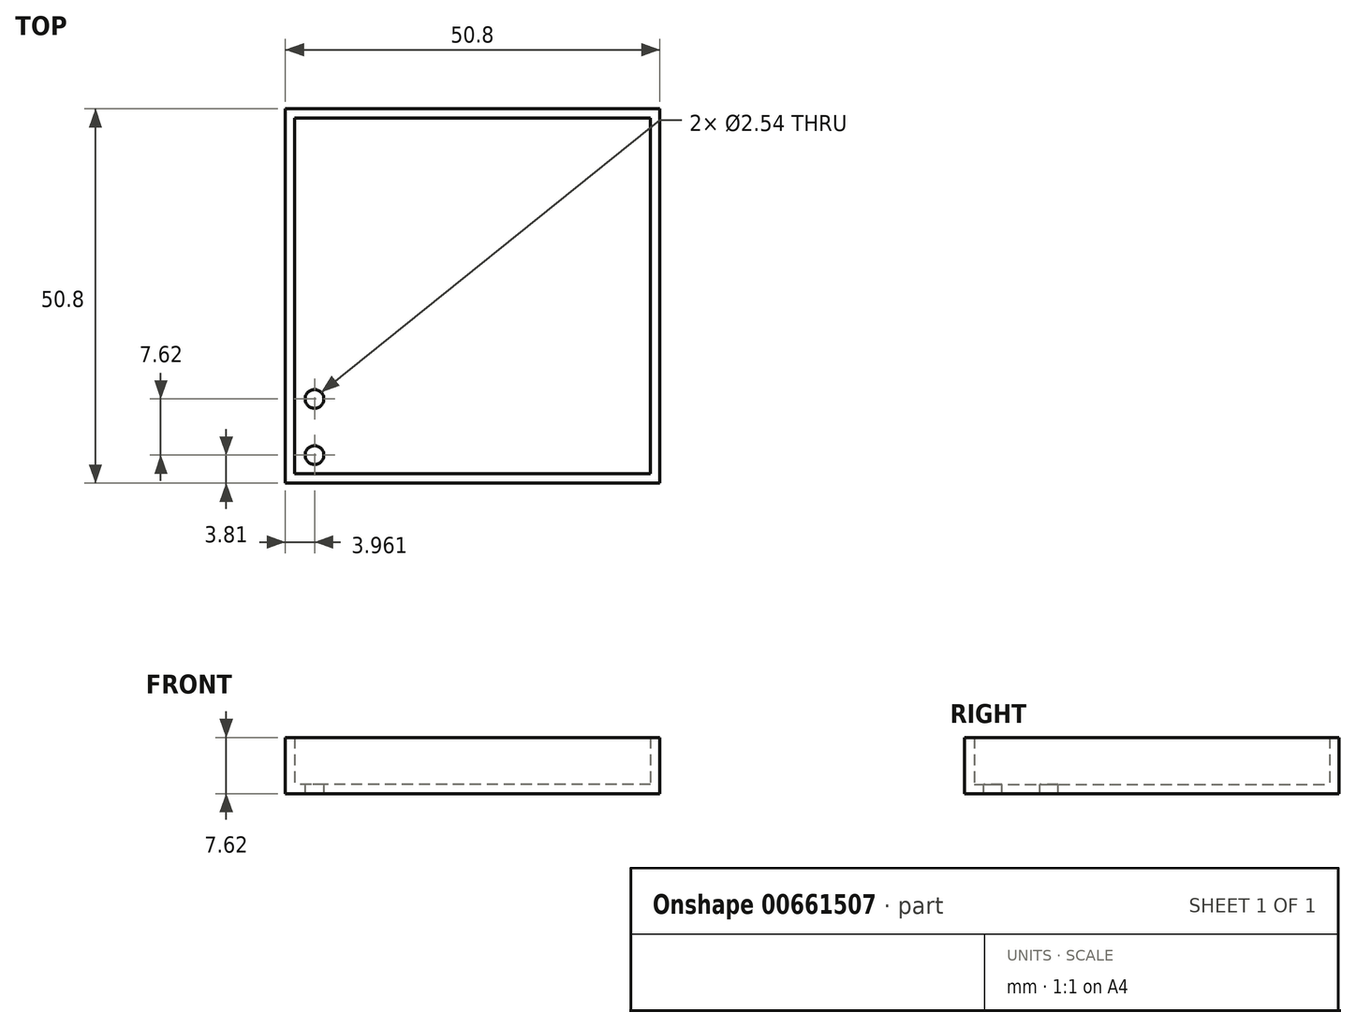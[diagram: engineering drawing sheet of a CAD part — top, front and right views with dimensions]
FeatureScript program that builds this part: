
annotation { "Feature Type Name" : "Feature", "Feature Type Description" : "" }
export const myFeature = defineFeature(function(context is Context, id is Id, definition is map)
    precondition{}
    {
        {
            var Q0;
            Q0=qCreatedBy(makeId("Top.planeOp"),FACE);
            var sketch = newSketch(context, id + "F0", { "sketchPlane" : qUnion([Q0])});
            skLineSegment(sketch, "E0.bottom", {"start": v(0, 0) * mm, "end": v(-50.8, 0) * mm});
            skLineSegment(sketch, "E0.top", {"start": v(0, 50.8) * mm, "end": v(-50.8, 50.8) * mm});
            skLineSegment(sketch, "E0.left", {"start": v(0, 0) * mm, "end": v(0, 50.8) * mm});
            skLineSegment(sketch, "E0.right", {"start": v(-50.8, 0) * mm, "end": v(-50.8, 50.8) * mm});
            skSolve(sketch);
        }
        {
            var Q0;
            Q0=makeQuery(id+"F0.imprint","IMPRINT",FACE,{"disambiguationData":[TD([[makeQuery(id+"F0.imprint","IMPRINT",EDGE,{"derivedFrom":sQuery(id+"F0.wireOp",EDGE,"E0.bottom")}),-1.0]])]});
            extrude(context, id + "F1", {"entities" : qUnion([Q0]), "depth" : 7.62 * mm, "offsetDistance" : 25.4 * mm});
        }
        {
            var Q0;
            Q0=makeQuery(id+"F1.opExtrude","CAP_FACE",FACE,{"disambiguationData":[OSD([sQuery(id+"F0.wireOp",EDGE,"E0.bottom"),sQuery(id+"F0.wireOp",EDGE,"E0.top"),sQuery(id+"F0.wireOp",EDGE,"E0.left"),sQuery(id+"F0.wireOp",EDGE,"E0.right")])],"isStart":false});
            shell(context, id + "F2", {"entities" : qUnion([Q0]), "thickness" : 1.27 * mm});
        }
        {
            var Q0;
            Q0=makeQuery(id+"F2.opShell","OFFSET_FACE",FACE,{"disambiguationData":[OSD([sQuery(id+"F0.wireOp",EDGE,"E0.bottom"),sQuery(id+"F0.wireOp",EDGE,"E0.top"),sQuery(id+"F0.wireOp",EDGE,"E0.left"),sQuery(id+"F0.wireOp",EDGE,"E0.right")])]});
            var sketch = newSketch(context, id + "F3", { "sketchPlane" : qUnion([Q0])});
            skLineSegment(sketch, "E1", {"start": v(-46.84, 1.27) * mm, "end": v(-46.84, 3.81) * mm});
            skCircle(sketch, "E2", {"center": v(-46.84, 3.81) * mm, "radius": 1.27 * mm});
            skLineSegment(sketch, "E3", {"start": v(-46.84, 3.81) * mm, "end": v(-46.84, 11.43) * mm});
            skCircle(sketch, "E4", {"center": v(-46.84, 11.43) * mm, "radius": 1.27 * mm});
            skSolve(sketch);
        }
        {
            var Q0;
            Q0=makeQuery(id+"F3.imprint","IMPRINT",FACE,{"disambiguationData":[TD([[makeQuery(id+"F3.imprint","IMPRINT",EDGE,{"derivedFrom":sQuery(id+"F3.wireOp",EDGE,"E4")}),1.0]])]});
            var Q1;
            {var subQ0=sQuery(id+"F3.wireOp",EDGE,"E3");var subQ1=sQuery(id+"F3.wireOp",EDGE,"E1");var subQ2=makeQuery(id+"F3.imprint","INTERSECT",VERTEX,{"derivedFrom":[subQ1,subQ0]});Q1=makeQuery(id+"F3.imprint","IMPRINT",FACE,{"disambiguationData":[TD([[makeQuery(id+"F3.imprint","IMPRINT",EDGE,{"disambiguationData":[TD([[subQ2,1.0]])],"derivedFrom":subQ1}),1.0]])]});}
            var Q2;
            {var subQ0=sQuery(id+"F3.wireOp",EDGE,"E3");var subQ1=sQuery(id+"F3.wireOp",EDGE,"E1");var subQ2=makeQuery(id+"F3.imprint","INTERSECT",VERTEX,{"derivedFrom":[subQ1,subQ0]});Q2=makeQuery(id+"F3.imprint","IMPRINT",FACE,{"disambiguationData":[TD([[makeQuery(id+"F3.imprint","IMPRINT",EDGE,{"disambiguationData":[TD([[subQ2,1.0]])],"derivedFrom":subQ1}),-1.0]])]});}
            extrude(context, id + "F4", {"entities" : qUnion([Q0, Q1, Q2]), "operationType" : NewBodyOperationType.REMOVE, "oppositeDirection" : true, "depth" : 25.4 * mm, "offsetDistance" : 25.4 * mm});
        }
    });
